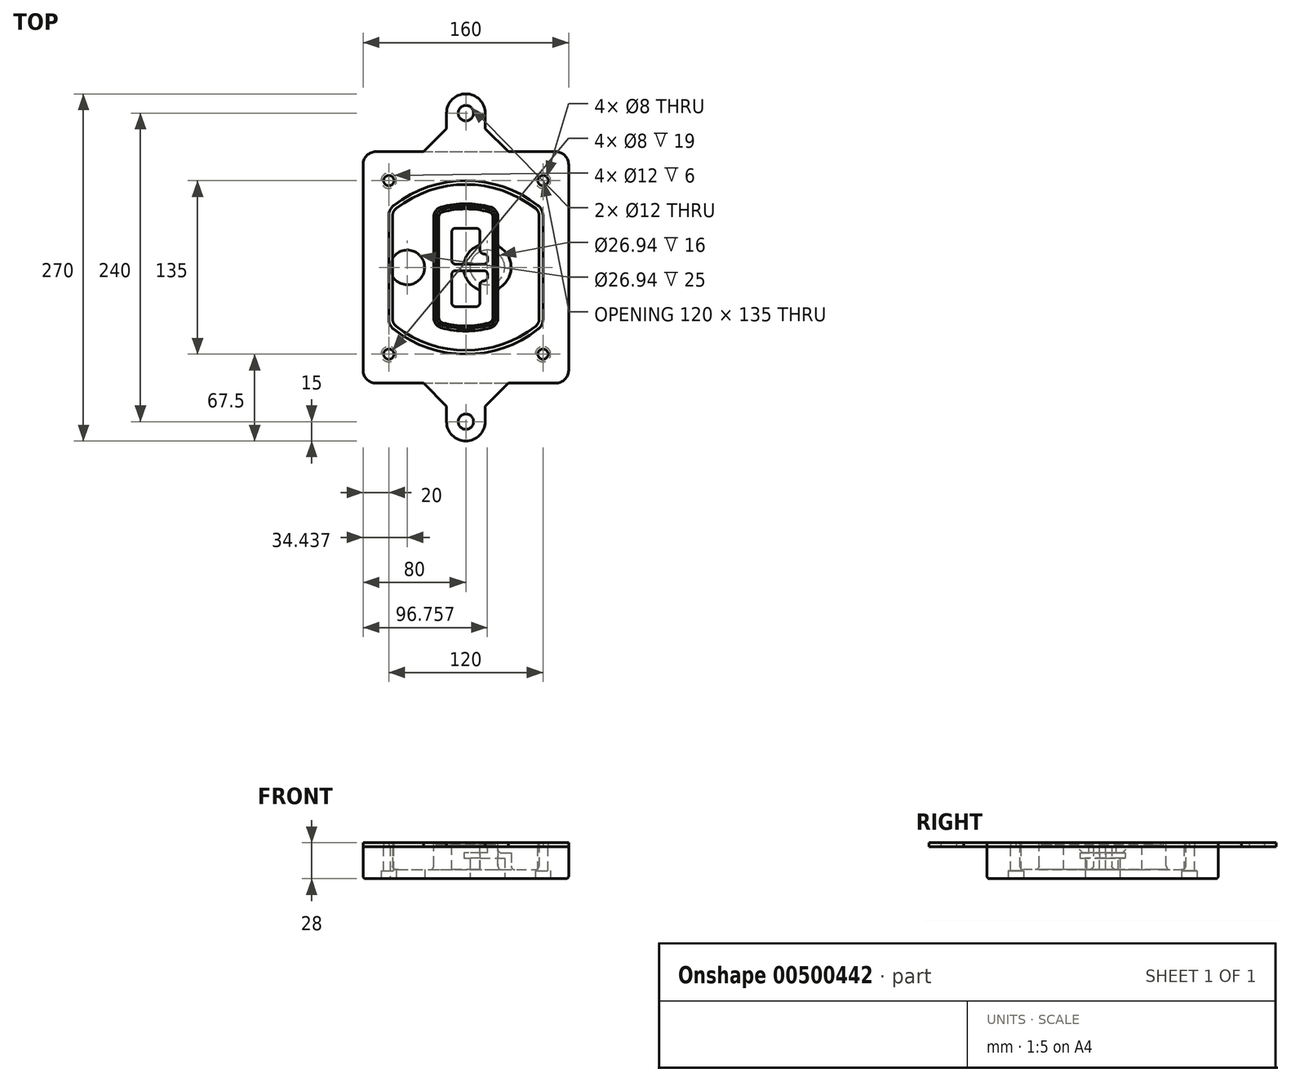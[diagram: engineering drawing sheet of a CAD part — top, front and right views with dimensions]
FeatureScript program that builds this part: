
annotation { "Feature Type Name" : "Feature", "Feature Type Description" : "" }
export const myFeature = defineFeature(function(context is Context, id is Id, definition is map)
    precondition{}
    {
        {
            var Q0;
            Q0=qCreatedBy(makeId("Top.planeOp"),FACE);
            var sketch = newSketch(context, id + "F0", { "sketchPlane" : qUnion([Q0])});
            skPoint(sketch, "E0.rect.middle", {"position": v(0, 0) * mm});
            skLineSegment(sketch, "E1.bottom", {"start": v(-70, -90) * mm, "end": v(70, -90) * mm});
            skLineSegment(sketch, "E1.top", {"start": v(-70, 90) * mm, "end": v(70, 90) * mm});
            skLineSegment(sketch, "E1.left", {"start": v(-80, -80) * mm, "end": v(-80, 80) * mm});
            skLineSegment(sketch, "E1.right", {"start": v(80, -80) * mm, "end": v(80, 80) * mm});
            skLineSegment(sketch, "E2", {"start": v(-80, 90) * mm, "end": v(80, -90) * mm, "construction": true});
            skLineSegment(sketch, "E3", {"start": v(80, 90) * mm, "end": v(-80, -90) * mm, "construction": true});
            skCircle(sketch, "E4", {"center": v(-60, 67.5) * mm, "radius": 4 * mm});
            skCircle(sketch, "E5", {"center": v(60, 67.5) * mm, "radius": 4 * mm});
            skCircle(sketch, "E6", {"center": v(60, -67.5) * mm, "radius": 4 * mm});
            skCircle(sketch, "E7", {"center": v(-60, -67.5) * mm, "radius": 4 * mm});
            skLineSegment(sketch, "E8", {"start": v(-60, 67.5) * mm, "end": v(60, 67.5) * mm, "construction": true});
            skLineSegment(sketch, "E9", {"start": v(60, 67.5) * mm, "end": v(60, -67.5) * mm, "construction": true});
            skLineSegment(sketch, "E10", {"start": v(60, -67.5) * mm, "end": v(-60, -67.5) * mm, "construction": true});
            skLineSegment(sketch, "E11", {"start": v(-60, -67.5) * mm, "end": v(-60, 67.5) * mm, "construction": true});
            skLineSegment(sketch, "E12", {"start": v(-60, 40.3) * mm, "end": v(-60, -40.3) * mm});
            skLineSegment(sketch, "E13", {"start": v(60, 40.3) * mm, "end": v(60, -40.3) * mm});
            skArc(sketch, "E14", {"start": v(56.15, 48.18) * mm, "mid": v(0, 67.5) * mm, "end": v(-56.15, 48.18) * mm});
            skArc(sketch, "E15", {"start": v(-56.15, -48.18) * mm, "mid": v(0, -67.5) * mm, "end": v(56.15, -48.18) * mm});
            skLineSegment(sketch, "E16", {"start": v(-60, 0) * mm, "end": v(60, 0) * mm, "construction": true});
            skPoint(sketch, "E17.visualSharp", {"position": v(-60, -45) * mm});
            skArc(sketch, "E17.filletArc", {"start": v(-60, -40.3) * mm, "mid": v(-58.99, -44.68) * mm, "end": v(-56.15, -48.18) * mm});
            skPoint(sketch, "E18.visualSharp", {"position": v(-60, 45) * mm});
            skArc(sketch, "E18.filletArc", {"start": v(-56.15, 48.18) * mm, "mid": v(-58.99, 44.68) * mm, "end": v(-60, 40.3) * mm});
            skPoint(sketch, "E19.visualSharp", {"position": v(60, 45) * mm});
            skArc(sketch, "E19.filletArc", {"start": v(60, 40.3) * mm, "mid": v(58.99, 44.68) * mm, "end": v(56.15, 48.18) * mm});
            skPoint(sketch, "E20.visualSharp", {"position": v(60, -45) * mm});
            skArc(sketch, "E20.filletArc", {"start": v(56.15, -48.18) * mm, "mid": v(58.99, -44.68) * mm, "end": v(60, -40.3) * mm});
            skPoint(sketch, "E21.visualSharp", {"position": v(-80, 90) * mm});
            skArc(sketch, "E21.filletArc", {"start": v(-70, 90) * mm, "mid": v(-77.07, 87.07) * mm, "end": v(-80, 80) * mm});
            skPoint(sketch, "E22.visualSharp", {"position": v(80, 90) * mm});
            skArc(sketch, "E22.filletArc", {"start": v(80, 80) * mm, "mid": v(77.07, 87.07) * mm, "end": v(70, 90) * mm});
            skPoint(sketch, "E23.visualSharp", {"position": v(80, -90) * mm});
            skArc(sketch, "E23.filletArc", {"start": v(70, -90) * mm, "mid": v(77.07, -87.07) * mm, "end": v(80, -80) * mm});
            skPoint(sketch, "E24.visualSharp", {"position": v(-80, -90) * mm});
            skArc(sketch, "E24.filletArc", {"start": v(-80, -80) * mm, "mid": v(-77.07, -87.07) * mm, "end": v(-70, -90) * mm});
            skArc(sketch, "E25.0", {"start": v(57, 40.3) * mm, "mid": v(56.3, 43.36) * mm, "end": v(54.3, 45.81) * mm});
            skLineSegment(sketch, "E25.1", {"start": v(57, 40.3) * mm, "end": v(57, -40.3) * mm});
            skArc(sketch, "E25.2", {"start": v(54.3, -45.81) * mm, "mid": v(56.3, -43.36) * mm, "end": v(57, -40.3) * mm});
            skArc(sketch, "E25.3", {"start": v(-54.3, -45.81) * mm, "mid": v(0, -64.5) * mm, "end": v(54.3, -45.81) * mm});
            skArc(sketch, "E25.4", {"start": v(-57, -40.3) * mm, "mid": v(-56.3, -43.36) * mm, "end": v(-54.3, -45.81) * mm});
            skArc(sketch, "E25.5", {"start": v(54.3, 45.81) * mm, "mid": v(0, 64.5) * mm, "end": v(-54.3, 45.81) * mm});
            skLineSegment(sketch, "E25.6", {"start": v(-57, 40.3) * mm, "end": v(-57, -40.3) * mm});
            skArc(sketch, "E25.7", {"start": v(-54.3, 45.81) * mm, "mid": v(-56.3, 43.36) * mm, "end": v(-57, 40.3) * mm});
            skArc(sketch, "E26.0", {"start": v(-58.62, 51.33) * mm, "mid": v(-62.58, 46.43) * mm, "end": v(-64, 40.3) * mm});
            skArc(sketch, "E26.1", {"start": v(58.62, 51.33) * mm, "mid": v(0, 71.5) * mm, "end": v(-58.62, 51.33) * mm});
            skArc(sketch, "E26.2", {"start": v(64, 40.3) * mm, "mid": v(62.58, 46.43) * mm, "end": v(58.62, 51.33) * mm});
            skLineSegment(sketch, "E26.3", {"start": v(64, 40.3) * mm, "end": v(64, -40.3) * mm});
            skArc(sketch, "E26.4", {"start": v(58.62, -51.33) * mm, "mid": v(62.58, -46.43) * mm, "end": v(64, -40.3) * mm});
            skLineSegment(sketch, "E26.5", {"start": v(-64, 40.3) * mm, "end": v(-64, -40.3) * mm});
            skArc(sketch, "E26.6", {"start": v(-58.62, -51.33) * mm, "mid": v(0, -71.5) * mm, "end": v(58.62, -51.33) * mm});
            skArc(sketch, "E26.7", {"start": v(-64, -40.3) * mm, "mid": v(-62.58, -46.43) * mm, "end": v(-58.62, -51.33) * mm});
            skSolve(sketch);
        }
        {
            var Q0;
            Q0=makeQuery(id+"F0.imprint","IMPRINT",FACE,{"disambiguationData":[TD([[makeQuery(id+"F0.imprint","IMPRINT",EDGE,{"derivedFrom":sQuery(id+"F0.wireOp",EDGE,"E1.bottom")}),1.0]])]});
            var Q1;
            Q1=makeQuery(id+"F0.imprint","IMPRINT",FACE,{"disambiguationData":[TD([[makeQuery(id+"F0.imprint","IMPRINT",EDGE,{"derivedFrom":sQuery(id+"F0.wireOp",EDGE,"E12")}),1.0]])]});
            var Q2;
            Q2=makeQuery(id+"F0.imprint","IMPRINT",FACE,{"disambiguationData":[TD([[makeQuery(id+"F0.imprint","IMPRINT",EDGE,{"derivedFrom":sQuery(id+"F0.wireOp",EDGE,"E25.0")}),1.0]])]});
            var Q3;
            Q3=makeQuery(id+"F0.imprint","IMPRINT",FACE,{"disambiguationData":[TD([[makeQuery(id+"F0.imprint","IMPRINT",EDGE,{"derivedFrom":sQuery(id+"F0.wireOp",EDGE,"E12")}),-1.0]])]});
            extrude(context, id + "F1", {"entities" : qUnion([Q0, Q1, Q2, Q3]), "oppositeDirection" : true, "depth" : 25 * mm});
        }
        {
            var Q0;
            Q0=makeQuery(id+"F0.imprint","IMPRINT",FACE,{"disambiguationData":[TD([[makeQuery(id+"F0.imprint","IMPRINT",EDGE,{"derivedFrom":sQuery(id+"F0.wireOp",EDGE,"E12")}),1.0]])]});
            extrude(context, id + "F2", {"entities" : qUnion([Q0]), "operationType" : NewBodyOperationType.ADD, "depth" : 3 * mm});
        }
        {
            var Q0;
            Q0=makeQuery(id+"F0.imprint","IMPRINT",FACE,{"disambiguationData":[TD([[makeQuery(id+"F0.imprint","IMPRINT",EDGE,{"derivedFrom":sQuery(id+"F0.wireOp",EDGE,"E25.0")}),1.0]])]});
            extrude(context, id + "F3", {"entities" : qUnion([Q0]), "operationType" : NewBodyOperationType.REMOVE, "oppositeDirection" : true, "depth" : 18 * mm});
        }
        {
            var Q0;
            Q0=makeQuery(id+"F2.opExtrude","CAP_FACE",FACE,{"disambiguationData":[OSD([sQuery(id+"F0.wireOp",EDGE,"E12"),sQuery(id+"F0.wireOp",EDGE,"E13"),sQuery(id+"F0.wireOp",EDGE,"E14"),sQuery(id+"F0.wireOp",EDGE,"E15"),sQuery(id+"F0.wireOp",EDGE,"E17.filletArc"),sQuery(id+"F0.wireOp",EDGE,"E18.filletArc"),sQuery(id+"F0.wireOp",EDGE,"E19.filletArc"),sQuery(id+"F0.wireOp",EDGE,"E20.filletArc"),sQuery(id+"F0.wireOp",EDGE,"E25.0"),sQuery(id+"F0.wireOp",EDGE,"E25.1"),sQuery(id+"F0.wireOp",EDGE,"E25.2"),sQuery(id+"F0.wireOp",EDGE,"E25.3"),sQuery(id+"F0.wireOp",EDGE,"E25.4"),sQuery(id+"F0.wireOp",EDGE,"E25.5"),sQuery(id+"F0.wireOp",EDGE,"E25.6"),sQuery(id+"F0.wireOp",EDGE,"E25.7")])],"isStart":false});
            var sketch = newSketch(context, id + "F4", { "sketchPlane" : qUnion([Q0])});
            skArc(sketch, "E27.0", {"start": v(-19.08, -46.97) * mm, "mid": v(0, -49.5) * mm, "end": v(19.08, -46.97) * mm});
            skArc(sketch, "E28.0", {"start": v(19.08, 46.97) * mm, "mid": v(0, 49.5) * mm, "end": v(-19.08, 46.97) * mm});
            skLineSegment(sketch, "E29", {"start": v(-25, 39.25) * mm, "end": v(-25, -39.25) * mm});
            skLineSegment(sketch, "E30", {"start": v(25, 39.25) * mm, "end": v(25, -39.25) * mm});
            skLineSegment(sketch, "E31", {"start": v(-25, 45.1) * mm, "end": v(25, 45.1) * mm, "construction": true});
            skLineSegment(sketch, "E32", {"start": v(-25, -45.1) * mm, "end": v(25, -45.1) * mm, "construction": true});
            skPoint(sketch, "E33.visualSharp", {"position": v(-25, 45.1) * mm});
            skArc(sketch, "E33.filletArc", {"start": v(-19.08, 46.97) * mm, "mid": v(-23.35, 44.11) * mm, "end": v(-25, 39.25) * mm});
            skPoint(sketch, "E34.visualSharp", {"position": v(25, 45.1) * mm});
            skArc(sketch, "E34.filletArc", {"start": v(25, 39.25) * mm, "mid": v(23.35, 44.11) * mm, "end": v(19.08, 46.97) * mm});
            skPoint(sketch, "E35.visualSharp", {"position": v(25, -45.1) * mm});
            skArc(sketch, "E35.filletArc", {"start": v(19.08, -46.97) * mm, "mid": v(23.35, -44.11) * mm, "end": v(25, -39.25) * mm});
            skPoint(sketch, "E36.visualSharp", {"position": v(-25, -45.1) * mm});
            skArc(sketch, "E36.filletArc", {"start": v(-25, -39.25) * mm, "mid": v(-23.35, -44.11) * mm, "end": v(-19.08, -46.97) * mm});
            skArc(sketch, "E37.0", {"start": v(54.3, 45.81) * mm, "mid": v(0, 64.5) * mm, "end": v(-54.3, 45.81) * mm});
            skArc(sketch, "E37.1", {"start": v(-54.3, 45.81) * mm, "mid": v(-56.3, 43.36) * mm, "end": v(-57, 40.3) * mm});
            skLineSegment(sketch, "E37.2", {"start": v(-57, 40.3) * mm, "end": v(-57, -40.3) * mm});
            skArc(sketch, "E37.3", {"start": v(-57, -40.3) * mm, "mid": v(-56.3, -43.36) * mm, "end": v(-54.3, -45.81) * mm});
            skArc(sketch, "E37.4", {"start": v(-54.3, -45.81) * mm, "mid": v(0, -64.5) * mm, "end": v(54.3, -45.81) * mm});
            skArc(sketch, "E37.5", {"start": v(54.3, -45.81) * mm, "mid": v(56.3, -43.36) * mm, "end": v(57, -40.3) * mm});
            skLineSegment(sketch, "E37.6", {"start": v(57, 40.3) * mm, "end": v(57, -40.3) * mm});
            skArc(sketch, "E37.7", {"start": v(57, 40.3) * mm, "mid": v(56.3, 43.36) * mm, "end": v(54.3, 45.81) * mm});
            skLineSegment(sketch, "E38.0", {"start": v(23, 39.25) * mm, "end": v(23, -39.25) * mm});
            skArc(sketch, "E38.1", {"start": v(18.56, -45.04) * mm, "mid": v(21.76, -42.9) * mm, "end": v(23, -39.25) * mm});
            skArc(sketch, "E38.2", {"start": v(-18.56, -45.04) * mm, "mid": v(0, -47.5) * mm, "end": v(18.56, -45.04) * mm});
            skArc(sketch, "E38.3", {"start": v(-23, -39.25) * mm, "mid": v(-21.76, -42.9) * mm, "end": v(-18.56, -45.04) * mm});
            skLineSegment(sketch, "E38.4", {"start": v(-23, 39.25) * mm, "end": v(-23, -39.25) * mm});
            skArc(sketch, "E38.5", {"start": v(23, 39.25) * mm, "mid": v(21.76, 42.9) * mm, "end": v(18.56, 45.04) * mm});
            skArc(sketch, "E38.6", {"start": v(-18.56, 45.04) * mm, "mid": v(-21.76, 42.9) * mm, "end": v(-23, 39.25) * mm});
            skArc(sketch, "E38.7", {"start": v(18.56, 45.04) * mm, "mid": v(0, 47.5) * mm, "end": v(-18.56, 45.04) * mm});
            skArc(sketch, "E39.0", {"start": v(21, 39.25) * mm, "mid": v(20.18, 41.68) * mm, "end": v(18.04, 43.1) * mm});
            skLineSegment(sketch, "E39.1", {"start": v(21, 39.25) * mm, "end": v(21, -39.25) * mm});
            skArc(sketch, "E39.2", {"start": v(18.04, -43.1) * mm, "mid": v(20.18, -41.68) * mm, "end": v(21, -39.25) * mm});
            skArc(sketch, "E39.3", {"start": v(-18.04, -43.1) * mm, "mid": v(0, -45.5) * mm, "end": v(18.04, -43.1) * mm});
            skArc(sketch, "E39.4", {"start": v(-21, -39.25) * mm, "mid": v(-20.18, -41.68) * mm, "end": v(-18.04, -43.1) * mm});
            skArc(sketch, "E39.5", {"start": v(18.04, 43.1) * mm, "mid": v(0, 45.5) * mm, "end": v(-18.04, 43.1) * mm});
            skLineSegment(sketch, "E39.6", {"start": v(-21, 39.25) * mm, "end": v(-21, -39.25) * mm});
            skArc(sketch, "E39.7", {"start": v(-18.04, 43.1) * mm, "mid": v(-20.18, 41.68) * mm, "end": v(-21, 39.25) * mm});
            skLineSegment(sketch, "E40", {"start": v(-25, 0) * mm, "end": v(25, 0) * mm, "construction": true});
            skLineSegment(sketch, "E41", {"start": v(-11, 5.5) * mm, "end": v(-11, 27.5) * mm});
            skLineSegment(sketch, "E42", {"start": v(-8, 30.5) * mm, "end": v(8, 30.5) * mm});
            skLineSegment(sketch, "E43", {"start": v(11, 27.5) * mm, "end": v(11, 13.5) * mm});
            skLineSegment(sketch, "E44", {"start": v(14, 10.5) * mm, "end": v(14, 10.5) * mm});
            skLineSegment(sketch, "E45", {"start": v(17, 7.5) * mm, "end": v(17, 5.5) * mm});
            skLineSegment(sketch, "E46", {"start": v(14, 2.5) * mm, "end": v(-8, 2.5) * mm});
            skPoint(sketch, "E47.visualSharp", {"position": v(-11, 30.5) * mm});
            skArc(sketch, "E47.filletArc", {"start": v(-8, 30.5) * mm, "mid": v(-10.12, 29.62) * mm, "end": v(-11, 27.5) * mm});
            skPoint(sketch, "E48.visualSharp", {"position": v(11, 30.5) * mm});
            skArc(sketch, "E48.filletArc", {"start": v(11, 27.5) * mm, "mid": v(10.12, 29.62) * mm, "end": v(8, 30.5) * mm});
            skPoint(sketch, "E49.visualSharp", {"position": v(11, 10.5) * mm});
            skArc(sketch, "E49.filletArc", {"start": v(11, 13.5) * mm, "mid": v(11.88, 11.38) * mm, "end": v(14, 10.5) * mm});
            skPoint(sketch, "E50.visualSharp", {"position": v(17, 10.5) * mm});
            skArc(sketch, "E50.filletArc", {"start": v(17, 7.5) * mm, "mid": v(16.12, 9.62) * mm, "end": v(14, 10.5) * mm});
            skPoint(sketch, "E51.visualSharp", {"position": v(17, 2.5) * mm});
            skArc(sketch, "E51.filletArc", {"start": v(14, 2.5) * mm, "mid": v(16.12, 3.38) * mm, "end": v(17, 5.5) * mm});
            skPoint(sketch, "E52.visualSharp", {"position": v(-11, 2.5) * mm});
            skArc(sketch, "E52.filletArc", {"start": v(-11, 5.5) * mm, "mid": v(-10.12, 3.38) * mm, "end": v(-8, 2.5) * mm});
            skLineSegment(sketch, "E53.0.MirrorCS", {"start": v(14, -2.5) * mm, "end": v(-8, -2.5) * mm});
            skArc(sketch, "E54.0.MirrorCS", {"start": v(-11, -5.5) * mm, "mid": v(-10.12, -3.38) * mm, "end": v(-8, -2.5) * mm});
            skLineSegment(sketch, "E55.0.MirrorCS", {"start": v(-11, -5.5) * mm, "end": v(-11, -27.5) * mm});
            skArc(sketch, "E56.0.MirrorCS", {"start": v(-8, -30.5) * mm, "mid": v(-10.12, -29.62) * mm, "end": v(-11, -27.5) * mm});
            skLineSegment(sketch, "E57.0.MirrorCS", {"start": v(-8, -30.5) * mm, "end": v(8, -30.5) * mm});
            skArc(sketch, "E58.0.MirrorCS", {"start": v(11, -27.5) * mm, "mid": v(10.12, -29.62) * mm, "end": v(8, -30.5) * mm});
            skLineSegment(sketch, "E59.0.MirrorCS", {"start": v(11, -27.5) * mm, "end": v(11, -13.5) * mm});
            skArc(sketch, "E60.0.MirrorCS", {"start": v(11, -13.5) * mm, "mid": v(11.88, -11.38) * mm, "end": v(14, -10.5) * mm});
            skArc(sketch, "E61.0.MirrorCS", {"start": v(17, -7.5) * mm, "mid": v(16.12, -9.62) * mm, "end": v(14, -10.5) * mm});
            skLineSegment(sketch, "E62.0.MirrorCS", {"start": v(17, -7.5) * mm, "end": v(17, -5.5) * mm});
            skArc(sketch, "E63.0.MirrorCS", {"start": v(14, -2.5) * mm, "mid": v(16.12, -3.38) * mm, "end": v(17, -5.5) * mm});
            skSolve(sketch);
        }
        {
            var Q0;
            Q0=makeQuery(id+"F4.imprint","IMPRINT",FACE,{"disambiguationData":[TD([[makeQuery(id+"F4.imprint","IMPRINT",EDGE,{"derivedFrom":sQuery(id+"F4.wireOp",EDGE,"E27.0")}),1.0]])]});
            var Q1;
            Q1=makeQuery(id+"F4.imprint","IMPRINT",FACE,{"disambiguationData":[TD([[makeQuery(id+"F4.imprint","IMPRINT",EDGE,{"derivedFrom":sQuery(id+"F4.wireOp",EDGE,"E38.0")}),-1.0]])]});
            var Q2;
            Q2=makeQuery(id+"F4.imprint","IMPRINT",FACE,{"disambiguationData":[TD([[makeQuery(id+"F4.imprint","IMPRINT",EDGE,{"derivedFrom":sQuery(id+"F4.wireOp",EDGE,"E39.0")}),1.0]])]});
            extrude(context, id + "F5", {"entities" : qUnion([Q0, Q1, Q2]), "operationType" : NewBodyOperationType.ADD, "endBound" : BoundingType.UP_TO_NEXT, "oppositeDirection" : true, "depth" : 25 * mm});
        }
        {
            var Q0;
            Q0=makeQuery(id+"F4.imprint","IMPRINT",FACE,{"disambiguationData":[TD([[makeQuery(id+"F4.imprint","IMPRINT",EDGE,{"derivedFrom":sQuery(id+"F4.wireOp",EDGE,"E38.0")}),-1.0]])]});
            extrude(context, id + "F6", {"entities" : qUnion([Q0]), "operationType" : NewBodyOperationType.REMOVE, "oppositeDirection" : true, "depth" : 2 * mm});
        }
        {
            var Q0;
            Q0=makeQuery(id+"F1.opExtrude","CAP_FACE",FACE,{"disambiguationData":[OSD([sQuery(id+"F0.wireOp",EDGE,"E1.bottom"),sQuery(id+"F0.wireOp",EDGE,"E1.top"),sQuery(id+"F0.wireOp",EDGE,"E1.left"),sQuery(id+"F0.wireOp",EDGE,"E1.right"),sQuery(id+"F0.wireOp",EDGE,"E4"),sQuery(id+"F0.wireOp",EDGE,"E5"),sQuery(id+"F0.wireOp",EDGE,"E6"),sQuery(id+"F0.wireOp",EDGE,"E7"),sQuery(id+"F0.wireOp",EDGE,"E21.filletArc"),sQuery(id+"F0.wireOp",EDGE,"E22.filletArc"),sQuery(id+"F0.wireOp",EDGE,"E23.filletArc"),sQuery(id+"F0.wireOp",EDGE,"E24.filletArc")])],"isStart":false});
            var sketch = newSketch(context, id + "F7", { "sketchPlane" : qUnion([Q0])});
            skCircle(sketch, "E64", {"center": v(16.76, 0) * mm, "radius": 13.47 * mm});
            skCircle(sketch, "E65", {"center": v(-45.56, 0) * mm, "radius": 13.47 * mm});
            skLineSegment(sketch, "E66", {"start": v(80, 0) * mm, "end": v(-80, 0) * mm});
            skCircle(sketch, "E67", {"center": v(16.76, 0) * mm, "radius": 18.47 * mm});
            skCircle(sketch, "E68", {"center": v(60, -67.5) * mm, "radius": 6 * mm});
            skCircle(sketch, "E69", {"center": v(-60, -67.5) * mm, "radius": 6 * mm});
            skCircle(sketch, "E70", {"center": v(-60, 67.5) * mm, "radius": 6 * mm});
            skCircle(sketch, "E71", {"center": v(60, 67.5) * mm, "radius": 6 * mm});
            skSolve(sketch);
        }
        {
            var Q0;
            {var subQ1=sQuery(id+"F7.wireOp",EDGE,"E66");var subQ4=sQuery(id+"F7.wireOp",EDGE,"E64");var subQ6=makeQuery(id+"F7.imprint","INTERSECT",VERTEX,{"disambiguationData":[OD(0.0)],"derivedFrom":[subQ4,subQ1]});Q0=makeQuery(id+"F7.imprint","IMPRINT",FACE,{"disambiguationData":[TD([[makeQuery(id+"F7.imprint","IMPRINT",EDGE,{"disambiguationData":[TD([[subQ6,-1.0]])],"derivedFrom":subQ4}),-1.0]])]});}
            var Q1;
            {var subQ0=sQuery(id+"F7.wireOp",EDGE,"E66");var subQ1=sQuery(id+"F7.wireOp",EDGE,"E64");var subQ3=makeQuery(id+"F7.imprint","INTERSECT",VERTEX,{"disambiguationData":[OD(0.0)],"derivedFrom":[subQ1,subQ0]});Q1=makeQuery(id+"F7.imprint","IMPRINT",FACE,{"disambiguationData":[TD([[makeQuery(id+"F7.imprint","IMPRINT",EDGE,{"disambiguationData":[TD([[subQ3,-1.0]])],"derivedFrom":subQ1}),1.0]])]});}
            var Q2;
            {var subQ0=sQuery(id+"F7.wireOp",EDGE,"E66");var subQ1=sQuery(id+"F7.wireOp",EDGE,"E64");var subQ3=makeQuery(id+"F7.imprint","INTERSECT",VERTEX,{"disambiguationData":[OD(0.0)],"derivedFrom":[subQ1,subQ0]});Q2=makeQuery(id+"F7.imprint","IMPRINT",FACE,{"disambiguationData":[TD([[makeQuery(id+"F7.imprint","IMPRINT",EDGE,{"disambiguationData":[TD([[subQ3,1.0]])],"derivedFrom":subQ1}),1.0]])]});}
            var Q3;
            {var subQ1=sQuery(id+"F7.wireOp",EDGE,"E66");var subQ4=sQuery(id+"F7.wireOp",EDGE,"E64");var subQ6=makeQuery(id+"F7.imprint","INTERSECT",VERTEX,{"disambiguationData":[OD(0.0)],"derivedFrom":[subQ4,subQ1]});Q3=makeQuery(id+"F7.imprint","IMPRINT",FACE,{"disambiguationData":[TD([[makeQuery(id+"F7.imprint","IMPRINT",EDGE,{"disambiguationData":[TD([[subQ6,1.0]])],"derivedFrom":subQ4}),-1.0]])]});}
            extrude(context, id + "F8", {"entities" : qUnion([Q0, Q1, Q2, Q3]), "operationType" : NewBodyOperationType.ADD, "oppositeDirection" : true, "depth" : 20 * mm});
        }
        {
            var Q0;
            {var subQ0=sQuery(id+"F7.wireOp",EDGE,"E66");var subQ1=sQuery(id+"F7.wireOp",EDGE,"E64");var subQ3=makeQuery(id+"F7.imprint","INTERSECT",VERTEX,{"disambiguationData":[OD(0.0)],"derivedFrom":[subQ1,subQ0]});Q0=makeQuery(id+"F7.imprint","IMPRINT",FACE,{"disambiguationData":[TD([[makeQuery(id+"F7.imprint","IMPRINT",EDGE,{"disambiguationData":[TD([[subQ3,-1.0]])],"derivedFrom":subQ1}),1.0]])]});}
            var Q1;
            {var subQ0=sQuery(id+"F7.wireOp",EDGE,"E66");var subQ1=sQuery(id+"F7.wireOp",EDGE,"E64");var subQ3=makeQuery(id+"F7.imprint","INTERSECT",VERTEX,{"disambiguationData":[OD(0.0)],"derivedFrom":[subQ1,subQ0]});Q1=makeQuery(id+"F7.imprint","IMPRINT",FACE,{"disambiguationData":[TD([[makeQuery(id+"F7.imprint","IMPRINT",EDGE,{"disambiguationData":[TD([[subQ3,1.0]])],"derivedFrom":subQ1}),1.0]])]});}
            extrude(context, id + "F9", {"entities" : qUnion([Q0, Q1]), "operationType" : NewBodyOperationType.REMOVE, "oppositeDirection" : true, "depth" : 16 * mm});
        }
        {
            var Q0;
            {var subQ0=sQuery(id+"F7.wireOp",EDGE,"E66");var subQ1=sQuery(id+"F7.wireOp",EDGE,"E65");var subQ3=makeQuery(id+"F7.imprint","INTERSECT",VERTEX,{"disambiguationData":[OD(0.0)],"derivedFrom":[subQ1,subQ0]});Q0=makeQuery(id+"F7.imprint","IMPRINT",FACE,{"disambiguationData":[TD([[makeQuery(id+"F7.imprint","IMPRINT",EDGE,{"disambiguationData":[TD([[subQ3,-1.0]])],"derivedFrom":subQ1}),1.0]])]});}
            var Q1;
            {var subQ0=sQuery(id+"F7.wireOp",EDGE,"E66");var subQ1=sQuery(id+"F7.wireOp",EDGE,"E65");var subQ3=makeQuery(id+"F7.imprint","INTERSECT",VERTEX,{"disambiguationData":[OD(0.0)],"derivedFrom":[subQ1,subQ0]});Q1=makeQuery(id+"F7.imprint","IMPRINT",FACE,{"disambiguationData":[TD([[makeQuery(id+"F7.imprint","IMPRINT",EDGE,{"disambiguationData":[TD([[subQ3,1.0]])],"derivedFrom":subQ1}),1.0]])]});}
            extrude(context, id + "F10", {"entities" : qUnion([Q0, Q1]), "operationType" : NewBodyOperationType.REMOVE, "oppositeDirection" : true, "depth" : 25 * mm});
        }
        {
            var Q0;
            Q0=makeQuery(id+"F9.boolean.opBoolean","COPY",FACE,{"derivedFrom":makeQuery(id+"F9.opExtrude","CAP_FACE",FACE,{"disambiguationData":[OSD([sQuery(id+"F7.wireOp",EDGE,"E64")])],"isStart":false})});
            var sketch = newSketch(context, id + "F11", { "sketchPlane" : qUnion([Q0])});
            skArc(sketch, "E72.0", {"start": v(11, 17.55) * mm, "mid": v(2.57, 11.82) * mm, "end": v(-1.54, 2.5) * mm});
            skArc(sketch, "E72.1", {"start": v(-1.54, -2.5) * mm, "mid": v(2.57, -11.82) * mm, "end": v(11, -17.55) * mm});
            skLineSegment(sketch, "E73", {"start": v(-1.54, -2.5) * mm, "end": v(14, -2.5) * mm});
            skLineSegment(sketch, "E74.0", {"start": v(14, 2.5) * mm, "end": v(-1.54, 2.5) * mm});
            skArc(sketch, "E74.1", {"start": v(14, 2.5) * mm, "mid": v(16.12, 3.38) * mm, "end": v(17, 5.5) * mm});
            skLineSegment(sketch, "E74.2", {"start": v(17, 7.5) * mm, "end": v(17, 5.5) * mm});
            skArc(sketch, "E74.3", {"start": v(17, 7.5) * mm, "mid": v(16.12, 9.62) * mm, "end": v(14, 10.5) * mm});
            skArc(sketch, "E74.4", {"start": v(11, 13.5) * mm, "mid": v(11.88, 11.38) * mm, "end": v(14, 10.5) * mm});
            skLineSegment(sketch, "E74.5", {"start": v(11, 17.55) * mm, "end": v(11, 13.5) * mm});
            skLineSegment(sketch, "E74.7", {"start": v(14, -2.5) * mm, "end": v(-1.54, -2.5) * mm});
            skArc(sketch, "E74.8", {"start": v(14, -2.5) * mm, "mid": v(16.12, -3.38) * mm, "end": v(17, -5.5) * mm});
            skLineSegment(sketch, "E74.9", {"start": v(17, -7.5) * mm, "end": v(17, -5.5) * mm});
            skArc(sketch, "E74.10", {"start": v(17, -7.5) * mm, "mid": v(16.12, -9.62) * mm, "end": v(14, -10.5) * mm});
            skArc(sketch, "E74.11", {"start": v(11, -13.5) * mm, "mid": v(11.88, -11.38) * mm, "end": v(14, -10.5) * mm});
            skLineSegment(sketch, "E74.12", {"start": v(11, -17.55) * mm, "end": v(11, -13.5) * mm});
            skPoint(sketch, "E75.orphan", {"position": v(11, -27.5) * mm});
            skPoint(sketch, "E76.orphan", {"position": v(-8, -2.5) * mm});
            skPoint(sketch, "E77.orphan", {"position": v(-8, 2.5) * mm});
            skPoint(sketch, "E78.orphan", {"position": v(11, 27.5) * mm});
            skSolve(sketch);
        }
        {
            var Q0;
            Q0=makeQuery(id+"F7.imprint","IMPRINT",FACE,{"disambiguationData":[TD([[makeQuery(id+"F7.imprint","IMPRINT",EDGE,{"derivedFrom":sQuery(id+"F7.wireOp",EDGE,"E68")}),1.0]])]});
            var Q1;
            Q1=makeQuery(id+"F7.imprint","IMPRINT",FACE,{"disambiguationData":[TD([[makeQuery(id+"F7.imprint","IMPRINT",EDGE,{"derivedFrom":makeQuery(id+"F1.opExtrude","CAP_EDGE",EDGE,{"disambiguationData":[OSD([sQuery(id+"F0.wireOp",EDGE,"E5")])],"isStart":false})}),-1.0]])]});
            var Q2;
            Q2=makeQuery(id+"F7.imprint","IMPRINT",FACE,{"disambiguationData":[TD([[makeQuery(id+"F7.imprint","IMPRINT",EDGE,{"derivedFrom":sQuery(id+"F7.wireOp",EDGE,"E69")}),1.0]])]});
            var Q3;
            Q3=makeQuery(id+"F7.imprint","IMPRINT",FACE,{"disambiguationData":[TD([[makeQuery(id+"F7.imprint","IMPRINT",EDGE,{"derivedFrom":makeQuery(id+"F1.opExtrude","CAP_EDGE",EDGE,{"disambiguationData":[OSD([sQuery(id+"F0.wireOp",EDGE,"E4")])],"isStart":false})}),-1.0]])]});
            var Q4;
            Q4=makeQuery(id+"F7.imprint","IMPRINT",FACE,{"disambiguationData":[TD([[makeQuery(id+"F7.imprint","IMPRINT",EDGE,{"derivedFrom":sQuery(id+"F7.wireOp",EDGE,"E70")}),1.0]])]});
            var Q5;
            Q5=makeQuery(id+"F7.imprint","IMPRINT",FACE,{"disambiguationData":[TD([[makeQuery(id+"F7.imprint","IMPRINT",EDGE,{"derivedFrom":makeQuery(id+"F1.opExtrude","CAP_EDGE",EDGE,{"disambiguationData":[OSD([sQuery(id+"F0.wireOp",EDGE,"E7")])],"isStart":false})}),-1.0]])]});
            var Q6;
            Q6=makeQuery(id+"F7.imprint","IMPRINT",FACE,{"disambiguationData":[TD([[makeQuery(id+"F7.imprint","IMPRINT",EDGE,{"derivedFrom":sQuery(id+"F7.wireOp",EDGE,"E71")}),1.0]])]});
            var Q7;
            Q7=makeQuery(id+"F7.imprint","IMPRINT",FACE,{"disambiguationData":[TD([[makeQuery(id+"F7.imprint","IMPRINT",EDGE,{"derivedFrom":makeQuery(id+"F1.opExtrude","CAP_EDGE",EDGE,{"disambiguationData":[OSD([sQuery(id+"F0.wireOp",EDGE,"E6")])],"isStart":false})}),-1.0]])]});
            extrude(context, id + "F12", {"entities" : qUnion([Q0, Q1, Q2, Q3, Q4, Q5, Q6, Q7]), "operationType" : NewBodyOperationType.REMOVE, "oppositeDirection" : true, "depth" : 6 * mm});
        }
        {
            var Q0;
            {var subQ7=sQuery(id+"F11.wireOp",EDGE,"E72.0");var subQ14=sQuery(id+"F11.wireOp",EDGE,"E72.1");var subQ16=sQuery(id+"F11.wireOp",EDGE,"E74.1");var subQ18=sQuery(id+"F11.wireOp",EDGE,"E74.8");Q0=qUnion([makeQuery(id+"F11.imprint","IMPRINT",FACE,{"disambiguationData":[TD([[makeQuery(id+"F11.imprint","IMPRINT",EDGE,{"derivedFrom":subQ7}),1.0]])]}),makeQuery(id+"F11.imprint","IMPRINT",FACE,{"disambiguationData":[TD([[makeQuery(id+"F11.imprint","IMPRINT",EDGE,{"derivedFrom":subQ14}),1.0]])]}),makeQuery(id+"F11.imprint","IMPRINT",FACE,{"disambiguationData":[TD([[makeQuery(id+"F11.imprint","IMPRINT",EDGE,{"derivedFrom":subQ16}),1.0]])]}),makeQuery(id+"F11.imprint","IMPRINT",FACE,{"disambiguationData":[TD([[makeQuery(id+"F11.imprint","IMPRINT",EDGE,{"derivedFrom":subQ18}),-1.0]])]})]);}
            var Q1;
            Q1=makeQuery(id+"F5.boolean.opBoolean","SPLIT",FACE,{"disambiguationData":[TD([makeQuery(id+"F5.opExtrude","SWEPT_FACE",FACE,{"disambiguationData":[OSD([sQuery(id+"F4.wireOp",EDGE,"E41")])]})])],"derivedFrom":makeQuery(id+"F3.boolean.opBoolean","COPY",FACE,{"derivedFrom":makeQuery(id+"F3.opExtrude","CAP_FACE",FACE,{"disambiguationData":[OSD([sQuery(id+"F0.wireOp",EDGE,"E25.0"),sQuery(id+"F0.wireOp",EDGE,"E25.1"),sQuery(id+"F0.wireOp",EDGE,"E25.2"),sQuery(id+"F0.wireOp",EDGE,"E25.3"),sQuery(id+"F0.wireOp",EDGE,"E25.4"),sQuery(id+"F0.wireOp",EDGE,"E25.5"),sQuery(id+"F0.wireOp",EDGE,"E25.6"),sQuery(id+"F0.wireOp",EDGE,"E25.7")])],"isStart":false})})});
            extrude(context, id + "F13", {"entities" : qUnion([Q0]), "operationType" : NewBodyOperationType.REMOVE, "endBound" : BoundingType.UP_TO_SURFACE, "endBoundEntityFace" : qUnion([Q1]), "depth" : 25 * mm});
        }
        {
            var Q0;
            Q0=makeQuery(id+"F3.boolean.opBoolean","COPY",EDGE,{"derivedFrom":makeQuery(id+"F3.opExtrude","CAP_EDGE",EDGE,{"disambiguationData":[OSD([sQuery(id+"F0.wireOp",EDGE,"E25.6")])],"isStart":false})});
            var Q1;
            Q1=makeQuery(id+"F8.boolean.opBoolean","INTERSECT",EDGE,{"derivedFrom":[makeQuery(id+"F5.opExtrude","SWEPT_FACE",FACE,{"disambiguationData":[OSD([sQuery(id+"F4.wireOp",EDGE,"E30")])]}),makeQuery(id+"F8.opExtrude","CAP_FACE",FACE,{"disambiguationData":[OSD([sQuery(id+"F7.wireOp",EDGE,"E67")])],"isStart":false})]});
            var Q2;
            Q2=makeQuery(id+"F8.boolean.opBoolean","INTERSECT",EDGE,{"disambiguationData":[OD(1.0)],"derivedFrom":[makeQuery(id+"F5.opExtrude","SWEPT_FACE",FACE,{"disambiguationData":[OSD([sQuery(id+"F4.wireOp",EDGE,"E30")])]}),makeQuery(id+"F8.opExtrude","SWEPT_FACE",FACE,{"disambiguationData":[OSD([sQuery(id+"F7.wireOp",EDGE,"E67")])]})]});
            var Q3;
            {var subQ0=sQuery(id+"F4.wireOp",EDGE,"E30");Q3=makeQuery(id+"F8.boolean.opBoolean","SPLIT",EDGE,{"disambiguationData":[TD([makeQuery(id+"F5.opExtrude","SWEPT_FACE",FACE,{"disambiguationData":[OSD([sQuery(id+"F4.wireOp",EDGE,"E35.filletArc")])]})])],"derivedFrom":makeQuery(id+"F5.opExtrude","CAP_EDGE",EDGE,{"disambiguationData":[OSD([subQ0])],"isStart":false})});}
            var Q4;
            {var subQ0=sQuery(id+"F0.wireOp",EDGE,"E25.7");var subQ1=sQuery(id+"F0.wireOp",EDGE,"E25.1");var subQ2=sQuery(id+"F0.wireOp",EDGE,"E25.6");var subQ3=sQuery(id+"F0.wireOp",EDGE,"E25.5");var subQ4=sQuery(id+"F0.wireOp",EDGE,"E25.4");var subQ5=sQuery(id+"F0.wireOp",EDGE,"E25.0");var subQ6=sQuery(id+"F0.wireOp",EDGE,"E25.2");var subQ7=sQuery(id+"F0.wireOp",EDGE,"E25.3");Q4=makeQuery(id+"F8.boolean.opBoolean","INTERSECT",EDGE,{"derivedFrom":[makeQuery(id+"F5.boolean.opBoolean","SPLIT",FACE,{"disambiguationData":[TD([makeQuery(id+"F2.opExtrude","SWEPT_FACE",FACE,{"disambiguationData":[OSD([subQ5])]})])],"derivedFrom":makeQuery(id+"F3.boolean.opBoolean","COPY",FACE,{"derivedFrom":makeQuery(id+"F3.opExtrude","CAP_FACE",FACE,{"disambiguationData":[OSD([subQ5,subQ1,subQ6,subQ7,subQ4,subQ3,subQ2,subQ0])],"isStart":false})})}),makeQuery(id+"F8.opExtrude","SWEPT_FACE",FACE,{"disambiguationData":[OSD([sQuery(id+"F7.wireOp",EDGE,"E67")])]})]});}
            var Q5;
            Q5=makeQuery(id+"F8.boolean.opBoolean","INTERSECT",EDGE,{"disambiguationData":[OD(0.0)],"derivedFrom":[makeQuery(id+"F5.opExtrude","SWEPT_FACE",FACE,{"disambiguationData":[OSD([sQuery(id+"F4.wireOp",EDGE,"E30")])]}),makeQuery(id+"F8.opExtrude","SWEPT_FACE",FACE,{"disambiguationData":[OSD([sQuery(id+"F7.wireOp",EDGE,"E67")])]})]});
            fillet(context, id + "F14", {"entities" : qUnion([Q0, Q1, Q2, Q3, Q4, Q5]), "radius" : 3 * mm, "tangentPropagation" : true, "allowEdgeOverflow" : false});
        }
        {
            var Q0;
            Q0=makeQuery(id+"F1.opExtrude","CAP_EDGE",EDGE,{"disambiguationData":[OSD([sQuery(id+"F0.wireOp",EDGE,"E1.bottom")])],"isStart":false});
            fillet(context, id + "F15", {"entities" : qUnion([Q0]), "radius" : 2 * mm, "tangentPropagation" : true, "allowEdgeOverflow" : false});
        }
        {
            var Q0;
            {var subQ0=sQuery(id+"F0.wireOp",EDGE,"E21.filletArc");var subQ1=sQuery(id+"F0.wireOp",EDGE,"E7");var subQ2=sQuery(id+"F0.wireOp",EDGE,"E6");var subQ3=sQuery(id+"F0.wireOp",EDGE,"E5");var subQ4=sQuery(id+"F0.wireOp",EDGE,"E4");var subQ5=sQuery(id+"F0.wireOp",EDGE,"E22.filletArc");var subQ6=sQuery(id+"F0.wireOp",EDGE,"E1.bottom");var subQ7=sQuery(id+"F0.wireOp",EDGE,"E1.right");var subQ8=sQuery(id+"F0.wireOp",EDGE,"E1.top");var subQ9=sQuery(id+"F0.wireOp",EDGE,"E1.left");var subQ10=sQuery(id+"F0.wireOp",EDGE,"E23.filletArc");var subQ11=sQuery(id+"F0.wireOp",EDGE,"E24.filletArc");Q0=makeQuery(id+"F2.boolean.opBoolean","SPLIT",FACE,{"disambiguationData":[TD([makeQuery(id+"F1.opExtrude","SWEPT_FACE",FACE,{"disambiguationData":[OSD([subQ6])]})])],"derivedFrom":makeQuery(id+"F1.opExtrude","CAP_FACE",FACE,{"disambiguationData":[OSD([subQ6,subQ8,subQ9,subQ7,subQ4,subQ3,subQ2,subQ1,subQ0,subQ5,subQ10,subQ11])],"isStart":true})});}
            var sketch = newSketch(context, id + "F16", { "sketchPlane" : qUnion([Q0])});
            skLineSegment(sketch, "E79", {"start": v(-33, 90) * mm, "end": v(-15, 108) * mm});
            skLineSegment(sketch, "E80", {"start": v(-15, 108) * mm, "end": v(-15, 120) * mm});
            skLineSegment(sketch, "E81", {"start": v(33, 90) * mm, "end": v(15, 108) * mm});
            skLineSegment(sketch, "E82", {"start": v(15, 120) * mm, "end": v(15, 108) * mm});
            skArc(sketch, "E83", {"start": v(15, 120) * mm, "mid": v(0, 135) * mm, "end": v(-15, 120) * mm});
            skCircle(sketch, "E84", {"center": v(0, 120) * mm, "radius": 6 * mm});
            skLineSegment(sketch, "E85", {"start": v(0, 120) * mm, "end": v(0, 90) * mm, "construction": true});
            skLineSegment(sketch, "E86", {"start": v(-80, 0) * mm, "end": v(80, 0) * mm, "construction": true});
            skLineSegment(sketch, "E87.MirrorCS", {"start": v(15, -120) * mm, "end": v(15, -108) * mm});
            skLineSegment(sketch, "E88.MirrorCS", {"start": v(0, -120) * mm, "end": v(0, -90) * mm, "construction": true});
            skCircle(sketch, "E89.MirrorC", {"center": v(0, -120) * mm, "radius": 6 * mm});
            skLineSegment(sketch, "E90.MirrorCS", {"start": v(-33, -90) * mm, "end": v(-15, -108) * mm});
            skLineSegment(sketch, "E91.MirrorCS", {"start": v(-15, -108) * mm, "end": v(-15, -120) * mm});
            skArc(sketch, "E92.MirrorCS", {"start": v(15, -120) * mm, "mid": v(0, -135) * mm, "end": v(-15, -120) * mm});
            skLineSegment(sketch, "E93", {"start": v(15, -108) * mm, "end": v(33, -90) * mm});
            skSolve(sketch);
        }
        {
            var Q0;
            {var subQ1=sQuery(id+"F16.wireOp",EDGE,"E79");Q0=makeQuery(id+"F16.imprint","IMPRINT",FACE,{"disambiguationData":[TD([[makeQuery(id+"F16.imprint","IMPRINT",EDGE,{"derivedFrom":subQ1}),-1.0]])]});}
            var Q1;
            Q1=makeQuery(id+"F16.imprint","IMPRINT",FACE,{"disambiguationData":[TD([[makeQuery(id+"F16.imprint","IMPRINT",EDGE,{"derivedFrom":makeQuery(id+"F1.opExtrude","CAP_EDGE",EDGE,{"disambiguationData":[OSD([sQuery(id+"F0.wireOp",EDGE,"E1.left")])],"isStart":true})}),-1.0]])]});
            var Q2;
            Q2=makeQuery(id+"F16.imprint","IMPRINT",FACE,{"disambiguationData":[TD([[makeQuery(id+"F16.imprint","IMPRINT",EDGE,{"derivedFrom":sQuery(id+"F16.wireOp",EDGE,"E87.MirrorCS")}),1.0]])]});
            var Q3;
            Q3=makeQuery(id+"F2.opExtrude","CAP_FACE",FACE,{"disambiguationData":[OSD([sQuery(id+"F0.wireOp",EDGE,"E12"),sQuery(id+"F0.wireOp",EDGE,"E13"),sQuery(id+"F0.wireOp",EDGE,"E14"),sQuery(id+"F0.wireOp",EDGE,"E15"),sQuery(id+"F0.wireOp",EDGE,"E17.filletArc"),sQuery(id+"F0.wireOp",EDGE,"E18.filletArc"),sQuery(id+"F0.wireOp",EDGE,"E19.filletArc"),sQuery(id+"F0.wireOp",EDGE,"E20.filletArc"),sQuery(id+"F0.wireOp",EDGE,"E25.0"),sQuery(id+"F0.wireOp",EDGE,"E25.1"),sQuery(id+"F0.wireOp",EDGE,"E25.2"),sQuery(id+"F0.wireOp",EDGE,"E25.3"),sQuery(id+"F0.wireOp",EDGE,"E25.4"),sQuery(id+"F0.wireOp",EDGE,"E25.5"),sQuery(id+"F0.wireOp",EDGE,"E25.6"),sQuery(id+"F0.wireOp",EDGE,"E25.7")])],"isStart":false});
            extrude(context, id + "F17", {"entities" : qUnion([Q0, Q1, Q2]), "endBound" : BoundingType.UP_TO_SURFACE, "endBoundEntityFace" : qUnion([Q3]), "depth" : 25 * mm});
        }
    });
